# Revit family: Modullaro ML 01
name_source: partatom
category: Meble
revit_build: Autodesk Revit 2018 (Build: 20190510_1515(x64)
units: mm (PartAtom-declared; Revit-internal decimal feet)

## family parameters
Numer OmniClass = 23.40.10.11.14
Obiekt nadrzędny = Powierzchnia
Punkt obliczania pomieszczeń = Nie
Tnij formami wycięć po wczytaniu = Nie
Tytuł OmniClass = Exterior Seating
Współdzielony = Nie

## types (1)
- Modullaro ML 01
    Domyślna rzędna = 1219 mm
    Długość = 1000 mm  [stored 3.28084 ft]
    IfcExportAs = IfcFurnishingElement
    Komentarze do typu = Ławka
    Materiał - informacja = Szeroki wybór kolorów wg palety RAL. Istnieje również możliwość specjalnego wykonania kolorystycznego na indywidualne zapytanie klienta.
    Model = Modullaro ML 01
    Obraz typu = ML-1.jpg
    Producent = Astrini Design
    Szerokość = 494 mm
    Temepratura użytkowania = -40°C do 80°C, ( -40°F do 176°F )
    URL = http://astrini-design.pl
    Waga (szacunkowo) = 16.00 kg
    Wysokość = 500 mm  [stored 1.64042 ft]

note: [stored X ft] marks values corroborated as IEEE doubles in the binary element streams (Revit-internal decimal feet)
